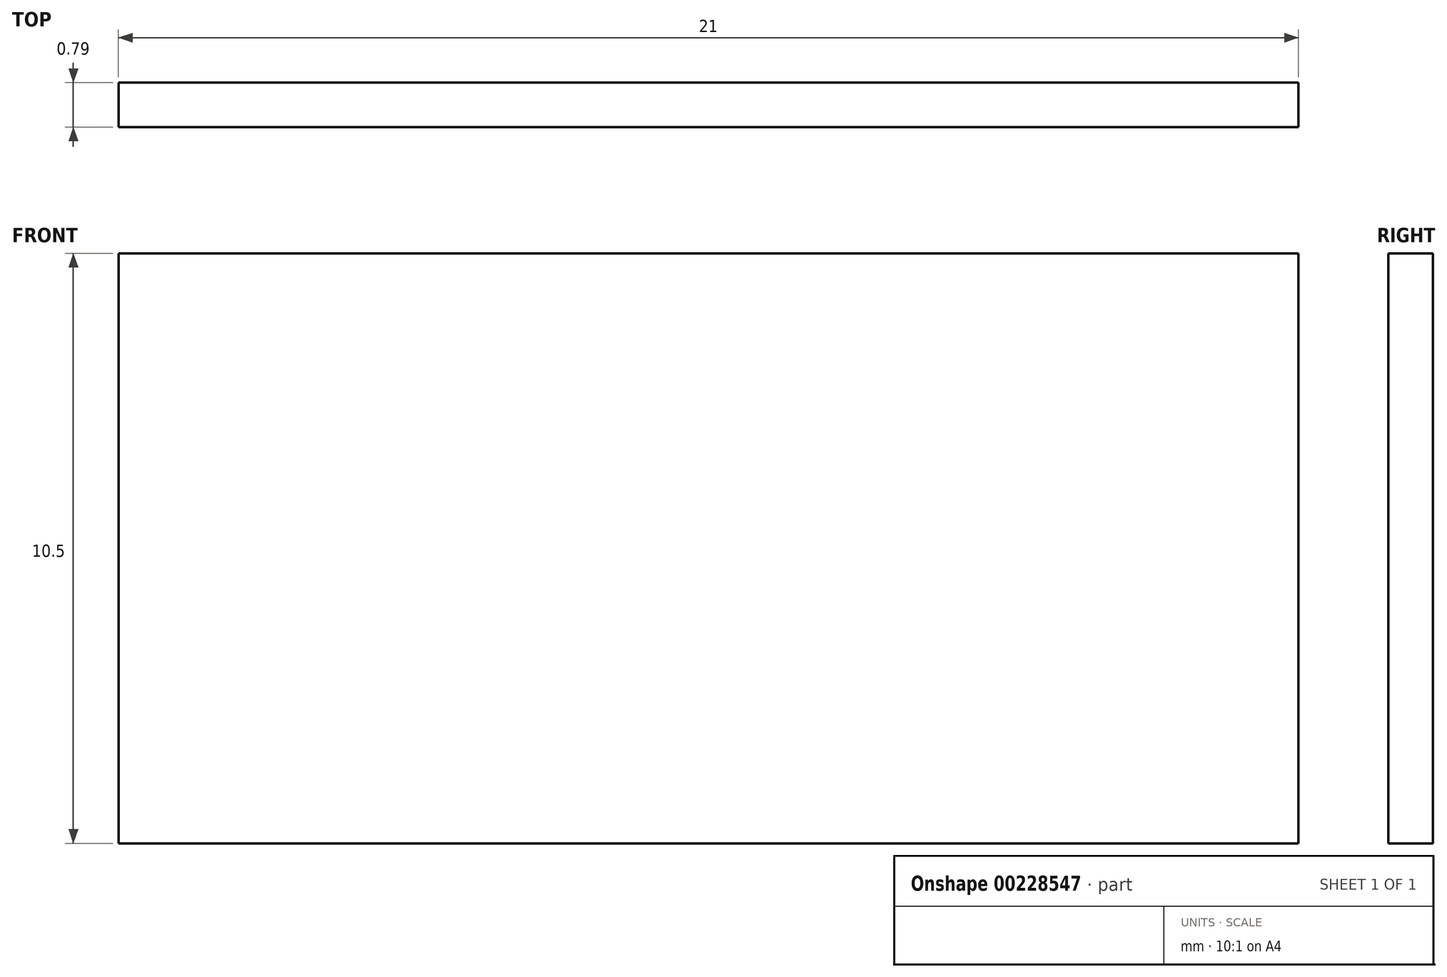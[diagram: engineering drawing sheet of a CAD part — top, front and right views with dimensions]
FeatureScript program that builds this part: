
annotation { "Feature Type Name" : "Feature", "Feature Type Description" : "" }
export const myFeature = defineFeature(function(context is Context, id is Id, definition is map)
    precondition{}
    {
        {
            var Q0;
            Q0=qCreatedBy(makeId("Front.planeOp"),FACE);
            var sketch = newSketch(context, id + "F0", { "sketchPlane" : qUnion([Q0])});
            skLineSegment(sketch, "E0.bottom", {"start": v(0, 0) * mm, "end": v(-1828.8, 0) * mm});
            skLineSegment(sketch, "E0.top", {"start": v(0, 914.4) * mm, "end": v(-1828.8, 914.4) * mm});
            skLineSegment(sketch, "E0.left", {"start": v(0, 0) * mm, "end": v(0, 914.4) * mm});
            skLineSegment(sketch, "E0.right", {"start": v(-1828.8, 0) * mm, "end": v(-1828.8, 914.4) * mm});
            skSolve(sketch);
        }
        {
            var Q0;
            Q0=makeQuery(id+"F0.imprint","IMPRINT",FACE,{"disambiguationData":[TD([[makeQuery(id+"F0.imprint","IMPRINT",EDGE,{"derivedFrom":sQuery(id+"F0.wireOp",EDGE,"E0.bottom")}),-1.0]])]});
            extrude(context, id + "F1", {"entities" : qUnion([Q0]), "depth" : 69.14 * mm});
        }
        {
            var Q0;
            Q0=makeQuery(id+"F1.opExtrude","SWEPT_BODY",BODY,{"disambiguationData":[OSD([sQuery(id+"F0.wireOp",EDGE,"E0.bottom"),sQuery(id+"F0.wireOp",EDGE,"E0.top"),sQuery(id+"F0.wireOp",EDGE,"E0.left"),sQuery(id+"F0.wireOp",EDGE,"E0.right")])]});
            var Q1;
            Q1=qCreatedBy(makeId("Origin.pointOp"),VERTEX);
            transform(context, id + "F2", {"entities" : qUnion([Q0]), "transformType" : TransformType.SCALE_UNIFORMLY, "scale" : 1 / 87.1, "scalePoint" : qUnion([Q1]), "makeCopy" : false});
        }
    });
